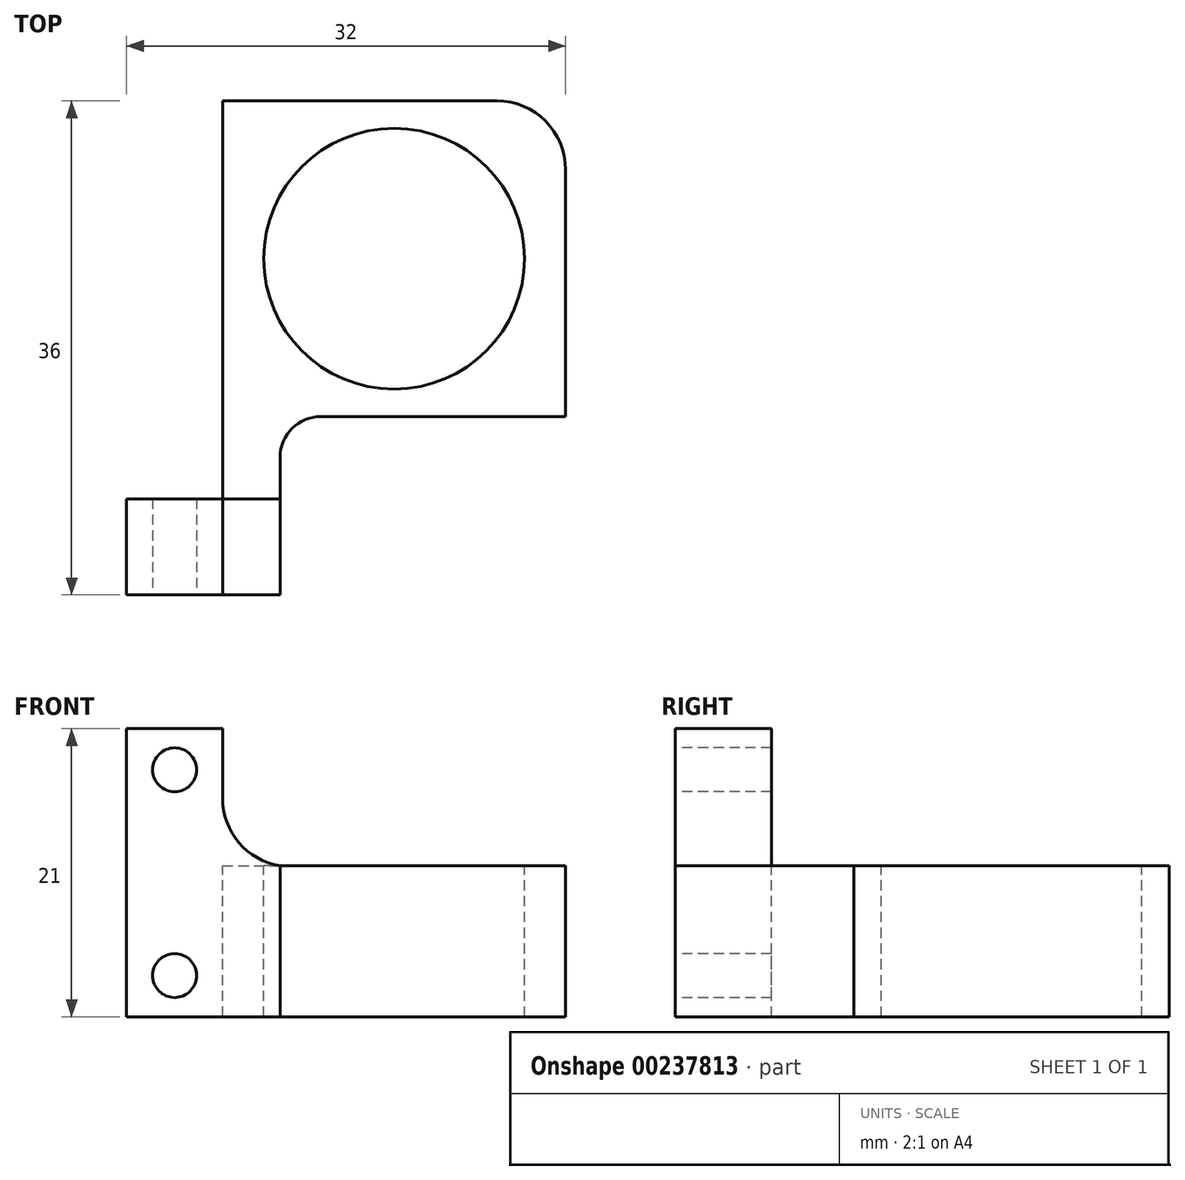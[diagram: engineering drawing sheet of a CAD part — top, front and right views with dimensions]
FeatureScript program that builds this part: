
annotation { "Feature Type Name" : "Feature", "Feature Type Description" : "" }
export const myFeature = defineFeature(function(context is Context, id is Id, definition is map)
    precondition{}
    {
        {
            var Q0;
            Q0=qCreatedBy(makeId("Top.planeOp"),FACE);
            var sketch = newSketch(context, id + "F0", { "sketchPlane" : qUnion([Q0])});
            skLineSegment(sketch, "E0.bottom", {"start": v(0, 0) * mm, "end": v(32, 0) * mm});
            skLineSegment(sketch, "E0.top", {"start": v(0, 36) * mm, "end": v(32, 36) * mm});
            skLineSegment(sketch, "E0.left", {"start": v(0, 0) * mm, "end": v(0, 36) * mm});
            skLineSegment(sketch, "E0.right", {"start": v(32, 0) * mm, "end": v(32, 36) * mm});
            skSolve(sketch);
        }
        {
            var Q0;
            Q0=qSketchRegion(id+"F0",true);
            extrude(context, id + "F1", {"entities" : qUnion([Q0]), "depth" : 4 * mm});
        }
        {
            var Q0;
            Q0=makeQuery(id+"F1.opExtrude","CAP_FACE",FACE,{"disambiguationData":[OSD([sQuery(id+"F0.wireOp",EDGE,"E0.bottom"),sQuery(id+"F0.wireOp",EDGE,"E0.top"),sQuery(id+"F0.wireOp",EDGE,"E0.left"),sQuery(id+"F0.wireOp",EDGE,"E0.right")])],"isStart":false});
            var sketch = newSketch(context, id + "F2", { "sketchPlane" : qUnion([Q0])});
            skCircle(sketch, "E1", {"center": v(19.5, 24.5) * mm, "radius": 9.5 * mm});
            skLineSegment(sketch, "E2.bottom", {"start": v(0, 36) * mm, "end": v(7, 36) * mm});
            skLineSegment(sketch, "E2.top", {"start": v(0, 7) * mm, "end": v(7, 7) * mm});
            skLineSegment(sketch, "E2.left", {"start": v(0, 36) * mm, "end": v(0, 7) * mm});
            skLineSegment(sketch, "E2.right", {"start": v(7, 36) * mm, "end": v(7, 7) * mm});
            skLineSegment(sketch, "E3.bottom", {"start": v(32, 0) * mm, "end": v(11.18, 0) * mm});
            skLineSegment(sketch, "E3.top", {"start": v(32, 13) * mm, "end": v(11.18, 13) * mm});
            skLineSegment(sketch, "E3.left", {"start": v(32, 0) * mm, "end": v(32, 13) * mm});
            skLineSegment(sketch, "E3.right", {"start": v(11.18, 0) * mm, "end": v(11.18, 13) * mm});
            skSolve(sketch);
        }
        {
            var Q0;
            Q0=qSketchRegion(id+"F2",true);
            extrude(context, id + "F3", {"entities" : qUnion([Q0]), "operationType" : NewBodyOperationType.REMOVE, "oppositeDirection" : true, "depth" : 25 * mm});
        }
        {
            var Q0;
            Q0=makeQuery(id+"F1.opExtrude","CAP_FACE",FACE,{"disambiguationData":[OSD([sQuery(id+"F0.wireOp",EDGE,"E0.bottom"),sQuery(id+"F0.wireOp",EDGE,"E0.top"),sQuery(id+"F0.wireOp",EDGE,"E0.left"),sQuery(id+"F0.wireOp",EDGE,"E0.right")])],"isStart":false});
            var sketch = newSketch(context, id + "F4", { "sketchPlane" : qUnion([Q0])});
            skLineSegment(sketch, "E4.bottom", {"start": v(0, 7) * mm, "end": v(7, 7) * mm});
            skLineSegment(sketch, "E4.top", {"start": v(0, 0) * mm, "end": v(7, 0) * mm});
            skLineSegment(sketch, "E4.left", {"start": v(0, 7) * mm, "end": v(0, 0) * mm});
            skLineSegment(sketch, "E4.right", {"start": v(7, 7) * mm, "end": v(7, 0) * mm});
            skSolve(sketch);
        }
        {
            var Q0;
            Q0=qSketchRegion(id+"F4",true);
            var Q1;
            {var subQ1=sQuery(id+"F4.wireOp",EDGE,"E4.right");Q1=makeQuery(id+"F4.imprint","IMPRINT",FACE,{"disambiguationData":[TD([[makeQuery(id+"F4.imprint","IMPRINT",EDGE,{"derivedFrom":subQ1}),1.0]])]});}
            extrude(context, id + "F5", {"entities" : qUnion([Q0, Q1]), "operationType" : NewBodyOperationType.ADD, "depth" : 7 * mm});
        }
        {
            var Q0;
            Q0=makeQuery(id+"F4.imprint","IMPRINT",FACE,{"disambiguationData":[TD([[makeQuery(id+"F4.imprint","IMPRINT",EDGE,{"derivedFrom":sQuery(id+"F4.wireOp",EDGE,"E4.bottom")}),-1.0]])]});
            extrude(context, id + "F6", {"entities" : qUnion([Q0]), "operationType" : NewBodyOperationType.ADD, "depth" : 17 * mm});
        }
        {
            var Q0;
            Q0=makeQuery(id+"F5.boolean.opBoolean","MERGE",FACE,{"derivedFrom":[makeQuery(id+"F1.opExtrude","SWEPT_FACE",FACE,{"disambiguationData":[OSD([sQuery(id+"F0.wireOp",EDGE,"E0.bottom")])]}),makeQuery(id+"F5.opExtrude","SWEPT_FACE",FACE,{"disambiguationData":[OSD([sQuery(id+"F4.wireOp",EDGE,"E4.top")])]})]});
            var sketch = newSketch(context, id + "F7", { "sketchPlane" : qUnion([Q0])});
            skLineSegment(sketch, "E5", {"start": v(3.5, 18) * mm, "end": v(3.5, 3) * mm});
            skCircle(sketch, "E6", {"center": v(3.5, 18) * mm, "radius": 1.6 * mm});
            skCircle(sketch, "E7", {"center": v(3.5, 3) * mm, "radius": 1.6 * mm});
            skLineSegment(sketch, "E8", {"start": v(7, 18) * mm, "end": v(0, 18) * mm, "construction": true});
            skSolve(sketch);
        }
        {
            var Q0;
            Q0=qSketchRegion(id+"F7",true);
            extrude(context, id + "F8", {"entities" : qUnion([Q0]), "operationType" : NewBodyOperationType.REMOVE, "oppositeDirection" : true, "depth" : 25 * mm});
        }
        {
            var Q0;
            Q0=makeQuery(id+"F1.opExtrude","SWEPT_EDGE",EDGE,{"disambiguationData":[OSD([sQuery(id+"F0.wireOp",EDGE,"E0.bottom"),sQuery(id+"F0.wireOp",EDGE,"E0.right")])]});
            var Q1;
            Q1=makeQuery(id+"F1.opExtrude","SWEPT_EDGE",EDGE,{"disambiguationData":[OSD([sQuery(id+"F0.wireOp",EDGE,"E0.top"),sQuery(id+"F0.wireOp",EDGE,"E0.right")])]});
            var Q2;
            Q2=makeQuery(id+"F3.boolean.opBoolean","COPY",EDGE,{"derivedFrom":makeQuery(id+"F3.opExtrude","SWEPT_EDGE",EDGE,{"disambiguationData":[OSD([sQuery(id+"F0.wireOp",EDGE,"E0.top"),sQuery(id+"F2.wireOp",EDGE,"E2.bottom"),sQuery(id+"F2.wireOp",EDGE,"E2.right")])]})});
            var Q3;
            Q3=makeQuery(id+"F3.boolean.opBoolean","COPY",EDGE,{"derivedFrom":makeQuery(id+"F3.opExtrude","SWEPT_EDGE",EDGE,{"disambiguationData":[OSD([sQuery(id+"F0.wireOp",EDGE,"E0.right"),sQuery(id+"F2.wireOp",EDGE,"E3.top"),sQuery(id+"F2.wireOp",EDGE,"E3.left")])]})});
            fillet(context, id + "F9", {"entities" : qUnion([Q0, Q1, Q2, Q3]), "radius" : 5 * mm, "tangentPropagation" : true, "allowEdgeOverflow" : false});
        }
        {
            var Q0;
            {var subQ0=sQuery(id+"F2.wireOp",EDGE,"E3.top");var subQ1=sQuery(id+"F2.wireOp",EDGE,"E3.right");Q0=makeQuery(id+"F5.boolean.opBoolean","MERGE",EDGE,{"derivedFrom":[makeQuery(id+"F3.boolean.opBoolean","COPY",EDGE,{"derivedFrom":makeQuery(id+"F3.opExtrude","SWEPT_EDGE",EDGE,{"disambiguationData":[OSD([subQ0,subQ1])]})}),makeQuery(id+"F5.opExtrude","SWEPT_EDGE",EDGE,{"disambiguationData":[OSD([subQ0,subQ1])]})]});}
            fillet(context, id + "F10", {"entities" : qUnion([Q0]), "radius" : 3 * mm, "tangentPropagation" : true, "allowEdgeOverflow" : false});
        }
        {
            var Q0;
            Q0=makeQuery(id+"F6.boolean.opBoolean","INTERSECT",EDGE,{"derivedFrom":[makeQuery(id+"F5.opExtrude","CAP_FACE",FACE,{"disambiguationData":[OSD([sQuery(id+"F0.wireOp",EDGE,"E0.bottom"),sQuery(id+"F0.wireOp",EDGE,"E0.top"),sQuery(id+"F0.wireOp",EDGE,"E0.right"),sQuery(id+"F2.wireOp",EDGE,"E1"),sQuery(id+"F2.wireOp",EDGE,"E2.right"),sQuery(id+"F2.wireOp",EDGE,"E3.top"),sQuery(id+"F2.wireOp",EDGE,"E3.right"),sQuery(id+"F4.wireOp",EDGE,"E4.bottom"),sQuery(id+"F4.wireOp",EDGE,"E4.top"),sQuery(id+"F4.wireOp",EDGE,"E4.left")])],"isStart":false}),makeQuery(id+"F6.opExtrude","SWEPT_FACE",FACE,{"disambiguationData":[OSD([sQuery(id+"F4.wireOp",EDGE,"E4.right")])]})]});
            fillet(context, id + "F11", {"entities" : qUnion([Q0]), "radius" : 5 * mm, "tangentPropagation" : true, "allowEdgeOverflow" : false});
        }
    });
